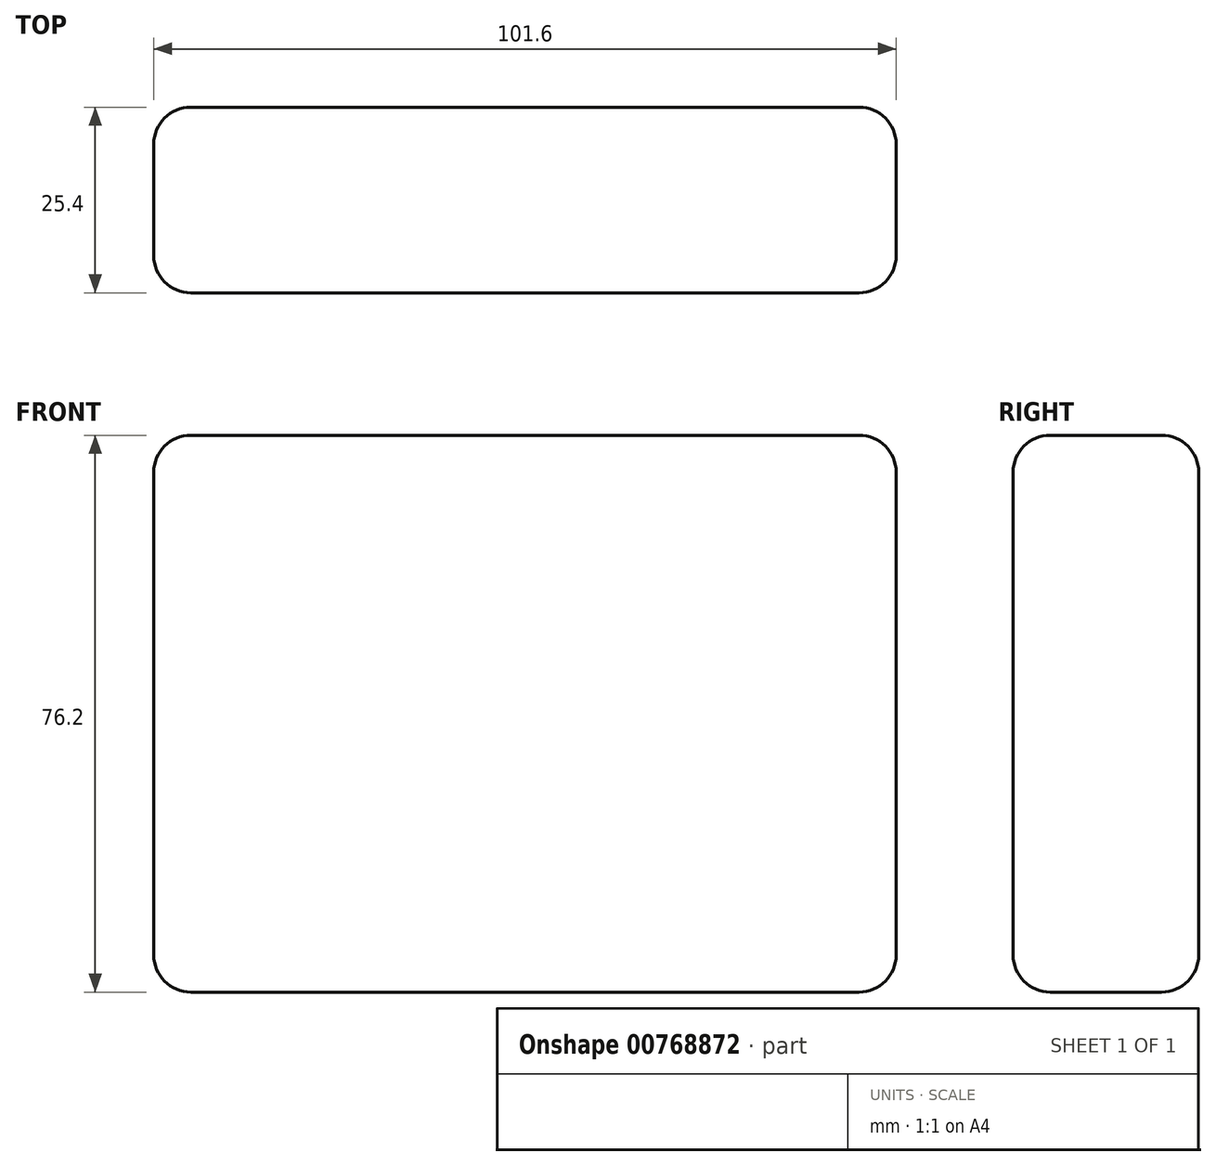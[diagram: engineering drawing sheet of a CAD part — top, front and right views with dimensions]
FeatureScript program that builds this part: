
annotation { "Feature Type Name" : "Feature", "Feature Type Description" : "" }
export const myFeature = defineFeature(function(context is Context, id is Id, definition is map)
    precondition{}
    {
        {
            var Q0;
            Q0=qCreatedBy(makeId("Front.planeOp"),FACE);
            var sketch = newSketch(context, id + "F0", { "sketchPlane" : qUnion([Q0])});
            skLineSegment(sketch, "E0.bottom", {"start": v(-50.8, -38.1) * mm, "end": v(50.8, -38.1) * mm});
            skLineSegment(sketch, "E0.top", {"start": v(-50.8, 38.1) * mm, "end": v(50.8, 38.1) * mm});
            skLineSegment(sketch, "E0.left", {"start": v(-50.8, -38.1) * mm, "end": v(-50.8, 38.1) * mm});
            skLineSegment(sketch, "E0.right", {"start": v(50.8, -38.1) * mm, "end": v(50.8, 38.1) * mm});
            skPoint(sketch, "E0.middle", {"position": v(0, 0) * mm});
            skSolve(sketch);
        }
        {
            var Q0;
            Q0 = qSketchRegion(id + "F0", true);
            extrude(context, id + "F1", {"entities" : qUnion([Q0]), "depth" : 25.4 * mm, "offsetDistance" : 25.4 * mm});
        }
        {
            var Q0;
            Q0=makeQuery(id+"F1.opExtrude","CAP_EDGE",EDGE,{"disambiguationData":[OSD([sQuery(id+"F0.wireOp",EDGE,"E0.top")])],"isStart":false});
            var Q1;
            Q1=makeQuery(id+"F1.opExtrude","CAP_EDGE",EDGE,{"disambiguationData":[OSD([sQuery(id+"F0.wireOp",EDGE,"E0.right")])],"isStart":false});
            var Q2;
            Q2=makeQuery(id+"F1.opExtrude","CAP_EDGE",EDGE,{"disambiguationData":[OSD([sQuery(id+"F0.wireOp",EDGE,"E0.bottom")])],"isStart":false});
            var Q3;
            Q3=makeQuery(id+"F1.opExtrude","CAP_EDGE",EDGE,{"disambiguationData":[OSD([sQuery(id+"F0.wireOp",EDGE,"E0.left")])],"isStart":false});
            var Q4;
            Q4=makeQuery(id+"F1.opExtrude","SWEPT_EDGE",EDGE,{"disambiguationData":[OSD([sQuery(id+"F0.wireOp",EDGE,"E0.top"),sQuery(id+"F0.wireOp",EDGE,"E0.left")])]});
            var Q5;
            Q5=makeQuery(id+"F1.opExtrude","CAP_EDGE",EDGE,{"disambiguationData":[OSD([sQuery(id+"F0.wireOp",EDGE,"E0.top")])],"isStart":true});
            var Q6;
            Q6=makeQuery(id+"F1.opExtrude","SWEPT_EDGE",EDGE,{"disambiguationData":[OSD([sQuery(id+"F0.wireOp",EDGE,"E0.top"),sQuery(id+"F0.wireOp",EDGE,"E0.right")])]});
            var Q7;
            Q7=makeQuery(id+"F1.opExtrude","CAP_EDGE",EDGE,{"disambiguationData":[OSD([sQuery(id+"F0.wireOp",EDGE,"E0.left")])],"isStart":true});
            var Q8;
            Q8=makeQuery(id+"F1.opExtrude","SWEPT_EDGE",EDGE,{"disambiguationData":[OSD([sQuery(id+"F0.wireOp",EDGE,"E0.bottom"),sQuery(id+"F0.wireOp",EDGE,"E0.left")])]});
            var Q9;
            Q9=makeQuery(id+"F1.opExtrude","SWEPT_FACE",FACE,{"disambiguationData":[OSD([sQuery(id+"F0.wireOp",EDGE,"E0.bottom")])]});
            var Q10;
            Q10=makeQuery(id+"F1.opExtrude","CAP_EDGE",EDGE,{"disambiguationData":[OSD([sQuery(id+"F0.wireOp",EDGE,"E0.right")])],"isStart":true});
            fillet(context, id + "F2", {"entities" : qUnion([Q0, Q1, Q2, Q3, Q4, Q5, Q6, Q7, Q8, Q9, Q10]), "radius" : 5.08 * mm, "tangentPropagation" : true, "allowEdgeOverflow" : false});
        }
    });
